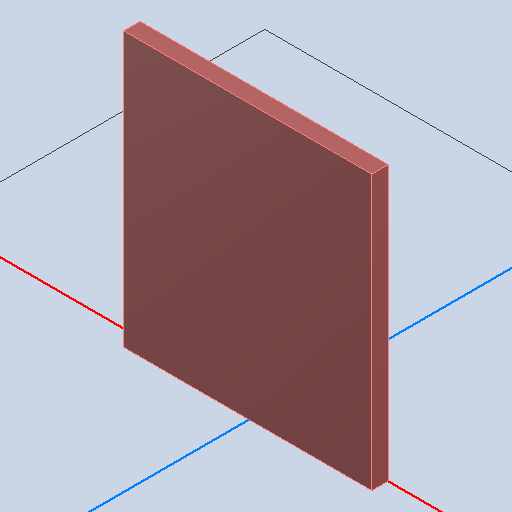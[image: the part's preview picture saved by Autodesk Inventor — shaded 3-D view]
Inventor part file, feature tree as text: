
AUTODESK INVENTOR PART (.ipt)
format: ipt  version: 2022 (Build 260153000, 153)  size: 94,208 bytes
history: native  units: mm
features: other x2, extrude x1
ambient origin geometry x8: Origin, YZ Plane, XZ Plane, XY Plane, X Axis, Y Axis, Z Axis, Center Point
bodies: Body1 (feature_tree)
feature tree (3):
  other  "Твердое тело1"
  extrude  "Выдавливание1"  Depth=1.0mm TaperAngle=0.0deg
  other  "LMZ13610, LMZ13610_30"
